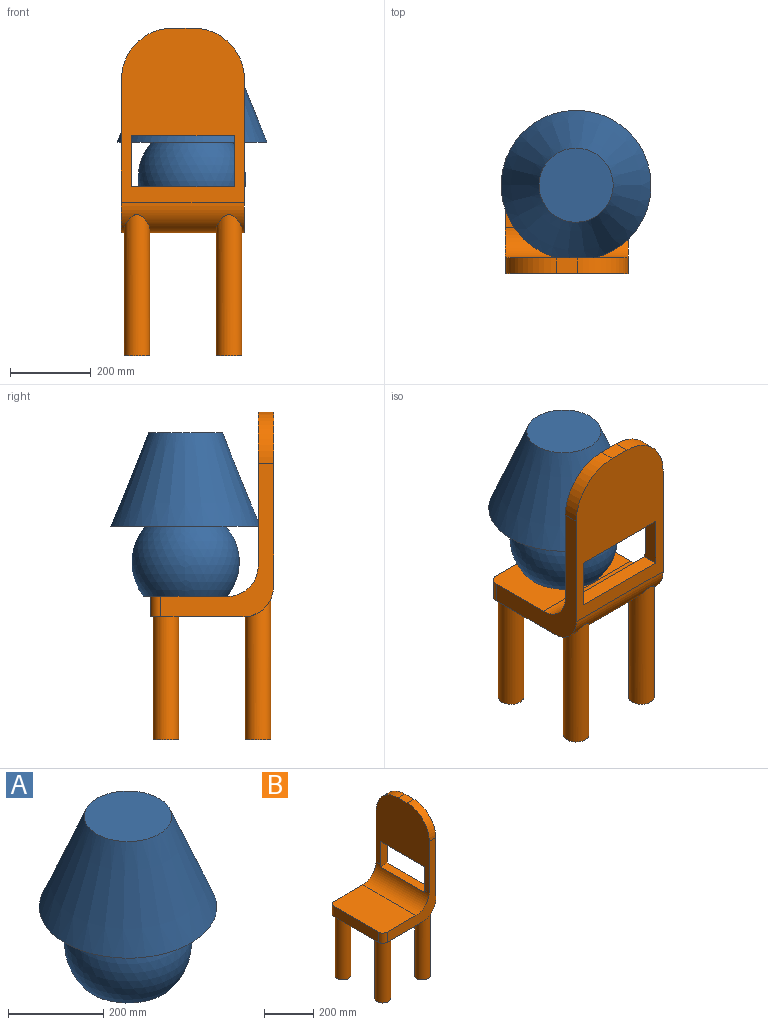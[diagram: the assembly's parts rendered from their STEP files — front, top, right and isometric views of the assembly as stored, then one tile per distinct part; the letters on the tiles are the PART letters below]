
ASSEMBLY  parts=2 mates=1
PART A: 5 faces, bbox 371.8x371.8x406.4 mm
  f0: plane 205.92x205.92mm, normal (0,0,-1), area 33304.2mm2, adj f4
  f1: plane 183.64x183.64mm, normal (0,0,1), area 26486.5mm2, adj f2
  f2: cone r=91.82mm half-angle=22deg, axis (0,0,-1), area 218918.4mm2, adj f1,f3
  f3: plane 371.76x371.76mm, normal (0,0,-1), area 77041.1mm2, adj f2,f4
  f4: sphere r=133.67mm, area 145936.5mm2, adj f0,f3
PART B: 26 faces, bbox 304.8x304.8x812.8 mm
  f0: plane 431.8x304.8mm, normal (1,0,0), area 92432mm2, adj f2,f3,f15,f16,f17,f18,f19,f20
  f1: plane 381x304.8mm, normal (-1,0,0), area 80174mm2, adj f2,f3,f15,f16,f17,f19,f20,f21
  f2: plane 381x279.4mm, normal (0,-1,0), area 26774.1mm2, adj f0,f1,f5,f6,f20,f22,f23,f25
  f3: plane 381x279.4mm, normal (0,1,0), area 26774.1mm2, adj f0,f1,f5,f6,f21,f22,f23,f24
  f4: plane 254x50.8mm, normal (-1,0,0), area 12903.2mm2, adj f5,f6,f24,f25
  f5: plane 304.8x190.5mm, normal (0,0,1), area 57787.5mm2, adj f2,f3,f4,f22,f24,f25
  f6: plane 304.8x228.6mm, normal (0,0,-1), area 63066.5mm2, adj f2,f3,f4,f7,f11,f23,f24,f25
  f7: cylinder r=31.75mm len=304.8mm, axis (0,0,1), area 60804.9mm2, adj f6,f8
  f8: plane 63.5x63.5mm, normal (0,0,-1), area 3166.9mm2, adj f7
  f9: cylinder r=31.75mm len=350.55mm, axis (0,0,1), area 64033.4mm2, adj f10,f23
  f10: plane 63.5x63.5mm, normal (0,0,-1), area 3166.9mm2, adj f9
  f11: cylinder r=31.75mm len=304.8mm, axis (0,0,1), area 60804.9mm2, adj f6,f12
  f12: plane 63.5x63.5mm, normal (0,0,-1), area 3166.9mm2, adj f11
  f13: cylinder r=31.75mm len=350.55mm, axis (0,0,1), area 64033.7mm2, adj f14,f23
  f14: plane 63.5x63.5mm, normal (0,0,-1), area 3166.9mm2, adj f13
  f15: plane 50.8x38.1mm, normal (0,0,1), area 1935.5mm2, adj f0,f1,f20,f21
  f16: plane 127x39.17mm, normal (0,-1,0), area 4843.2mm2, adj f0,f1,f17,f18,f22
  f17: plane 254x38.1mm, normal (0,0,-1), area 9677.4mm2, adj f0,f1,f16,f19
  f18: plane 254x39.17mm, normal (0,0,1), area 9948.1mm2, adj f0,f16,f19,f22
  f19: plane 127x39.17mm, normal (0,1,0), area 4843.2mm2, adj f0,f1,f17,f18,f22
  f20: cylinder r=127mm len=127mm, axis (-1,0,0), area 7600.6mm2, adj f0,f1,f2,f15
  f21: cylinder r=127mm len=127mm, axis (1,0,0), area 7600.6mm2, adj f0,f1,f3,f15
  f22: cylinder r=76.2mm len=304.8mm, axis (0,-1,0), area 33242mm2, adj f1,f2,f3,f5,f16,f18,f19
  f23: cylinder r=76.2mm len=304.8mm, axis (0,1,0), area 28574.2mm2, adj f0,f2,f3,f6,f9,f13
  f24: cylinder r=25.4mm len=50.8mm, axis (0,0,-1), area 2026.8mm2, adj f3,f4,f5,f6
  f25: cylinder r=25.4mm len=50.8mm, axis (0,0,1), area 2026.8mm2, adj f2,f4,f5,f6
PLACE A t=(22.64,9.42,0)mm
PLACE B rot(axis=(0,0,-1),90deg) t=(0,-56.72,-50.8)mm
MATE planar B.f5 <-> A.f2  axis (0,0,1) through (0,0,0)mm
